# Revit family: Elevation Mark Body_Square
name_source: partatom
category: Elevation Marks
revit_build: Autodesk Revit 2015 (Build: 20150512_1015(x64)
units: mm (PartAtom-declared; Revit-internal decimal feet)

## types (6) — shared parameters

## per-type parameters (varying)
| type | Bottom | Left | Right | Top |
| Filled Arrow | Elevation Mark Pointer_Square : Filled Arrow | Elevation Mark Pointer_Square : Filled Arrow | Elevation Mark Pointer_Square : Filled Arrow | Elevation Mark Pointer_Square : Filled Arrow |
| Detail Number and View Name | Elevation Mark Pointer_Square : Detail Number and View Name | Elevation Mark Pointer_Square : Detail Number and View Name | Elevation Mark Pointer_Square : Detail Number and View Name | Elevation Mark Pointer_Square : Detail Number and View Name |
| Detail Number | Elevation Mark Pointer_Square : Detail Number | Elevation Mark Pointer_Square : Detail Number | Elevation Mark Pointer_Square : Detail Number | Elevation Mark Pointer_Square : Detail Number |
| Filled Arrow and View Name | Elevation Mark Pointer_Square : Filled Arrow and View Name | Elevation Mark Pointer_Square : Filled Arrow and View Name | Elevation Mark Pointer_Square : Filled Arrow and View Name | Elevation Mark Pointer_Square : Filled Arrow and View Name |
| Filled Arrow and Detail Number | Elevation Mark Pointer_Square1 : Filled Arrow and Detail Number 2 | Elevation Mark Pointer_Square1 : Filled Arrow and Detail Number 2 | Elevation Mark Pointer_Square1 : Filled Arrow and Detail Number 2 | Elevation Mark Pointer_Square1 : Filled Arrow and Detail Number 2 |
| Detail Number Outside | Elevation Mark Pointer_Square : Detail Number | Elevation Mark Pointer_Square : Detail Number | Elevation Mark Pointer_Square : Detail Number | Elevation Mark Pointer_Square : Detail Number |

## geometry (parser evidence)
native form markers: Blend x2, Sweep x1
no freeform markers — native parametric forms only
